# Revit family: ВентКлиматСтрой Вентилятор систем дымоудаления осевой ВО-13-284ДУ
name_source: partatom
category: Оборудование
units: mm (PartAtom-declared; Revit-internal decimal feet)

## family parameters
Всегда вертикально = Да
Заголовок OmniClass = Fans for Air Ductwork
На основе рабочей плоскости = Нет
Номер OmniClass = 23.75.35.17.11
Общий = Нет
При загрузке вырезать с полостями = Нет
Размер круглого соединителя = Использовать диаметр
Тип детали = Вставляется
Точка расчета площади = Да

## types (22) — shared parameters
ADSK_Версия Revit = 2019
ADSK_Версия семейства = rev.1
ADSK_Единица измерения = шт.
ADSK_Классификация нагрузок = Прочее
ADSK_Количество = 1
ADSK_Количество фаз числовое = 3
ADSK_Коэффициент мощности = 0.8
ADSK_Предел огнестойкости = 120
Poles = 3
Размер символа УГО = 0.4
zero-valued in all types: ADSK_Материал тип подсчета

## per-type parameters (varying)
| type | A | B | B1 | D | D1 | De | H | L | R1 | Re | b | d | f | h | l | n | Полюсов |
| ВО 13-284-12К/*-4ДУ 4 полюса | 475 мм | 480 мм | 380 мм | 400 мм | 440 мм | 404 мм | 555 мм | 550 мм | 220 мм | 202 мм | 199 мм | 10 мм | 30 мм | 240 мм | 548 мм | 8 | 4 |
| ВО 13-284-12К/*-4ДУ 2 полюса | 475 мм | 480 мм | 380 мм | 400 мм | 440 мм | 404 мм | 555 мм | 550 мм | 220 мм | 202 мм | 199 мм | 10 мм | 30 мм | 240 мм | 548 мм | 8 | 2 |
| ВО 13-284-12К/*-4,5ДУ 4 полюса | 540 мм | 560 мм | 460 мм | 450 мм | 490 мм | 454 мм | 620 мм | 650 мм | 245 мм | 227 мм | 232 мм | 10 мм | 30 мм | 280 мм | 648 мм | 8 | 4 |
| ВО 13-284-12К/*-4,5ДУ 2 полюса | 540 мм | 560 мм | 460 мм | 450 мм | 490 мм | 454 мм | 620 мм | 650 мм | 245 мм | 227 мм | 232 мм | 10 мм | 30 мм | 280 мм | 648 мм | 8 | 2 |
| ВО 13-284-12К/*-5ДУ 4 полюса | 600 мм | 600 мм | 500 мм | 500 мм | 540 мм | 504 мм | 675 мм | 740 мм | 270 мм | 252 мм | 249 мм | 10 мм | 30 мм | 300 мм | 738 мм | 12 | 4 |
| ВО 13-284-12К/*-5ДУ 2 полюса | 600 мм | 600 мм | 500 мм | 500 мм | 540 мм | 504 мм | 675 мм | 740 мм | 270 мм | 252 мм | 249 мм | 10 мм | 30 мм | 300 мм | 738 мм | 12 | 2 |
| ВО 13-284-12К/*-5,6ДУ 4 полюса | 600 мм | 600 мм | 500 мм | 560 мм | 600 мм | 564 мм | 745 мм | 740 мм | 300 мм | 282 мм | 249 мм | 10 мм | 35 мм | 300 мм | 738 мм | 12 | 4 |
| ВО 13-284-12К/*-5,6ДУ 2 полюса | 600 мм | 600 мм | 500 мм | 560 мм | 600 мм | 564 мм | 745 мм | 740 мм | 300 мм | 282 мм | 249 мм | 10 мм | 35 мм | 300 мм | 738 мм | 12 | 2 |
| ВО 13-284-12К/*-6,3ДУ 4 полюса | 720 мм | 760 мм | 660 мм | 630 мм | 670 мм | 634 мм | 830 мм | 840 мм | 335 мм | 317 мм | 315 мм | 10 мм | 35 мм | 400 мм | 838 мм | 12 | 4 |
| ВО 13-284-12К/*-6,3ДУ 2 полюса | 720 мм | 760 мм | 660 мм | 630 мм | 670 мм | 634 мм | 830 мм | 840 мм | 335 мм | 317 мм | 315 мм | 10 мм | 35 мм | 400 мм | 838 мм | 12 | 2 |
| ВО 13-284-12К/*-7,1ДУ 6 полюсов | 900 мм | 900 мм | 800 мм | 710 мм | 750 мм | 714 мм | 925 мм | 930 мм | 375 мм | 357 мм | 373 мм | 10 мм | 35 мм | 450 мм | 928 мм | 16 | 6 |
| ВО 13-284-12К/*-7,1ДУ 4 полюса | 900 мм | 900 мм | 800 мм | 710 мм | 750 мм | 714 мм | 925 мм | 930 мм | 375 мм | 357 мм | 373 мм | 10 мм | 35 мм | 450 мм | 928 мм | 16 | 4 |
| ВО 13-284-12К/*-8ДУ 6 полюсов | 1000 мм | 1000 мм | 900 мм | 800 мм | 840 мм | 804 мм | 1020 мм | 1110 мм | 420 мм | 402 мм | 414 мм | 10 мм | 35 мм | 500 мм | 1108 мм | 16 | 6 |
| ВО 13-284-12К/*-8ДУ 4 полюса | 1000 мм | 1000 мм | 900 мм | 800 мм | 840 мм | 804 мм | 1020 мм | 1110 мм | 420 мм | 402 мм | 414 мм | 10 мм | 35 мм | 500 мм | 1108 мм | 16 | 4 |
| ВО 13-284-12К/*-9ДУ 6 полюсов | 1100 мм | 1100 мм | 1000 мм | 900 мм | 950 мм | 904 мм | 1135 мм | 1140 мм | 475 мм | 452 мм | 456 мм | 10 мм | 40 мм | 550 мм | 1138 мм | 16 | 6 |
| ВО 13-284-12К/*-9ДУ 4 полюса | 1100 мм | 1100 мм | 1000 мм | 900 мм | 950 мм | 904 мм | 1135 мм | 1140 мм | 475 мм | 452 мм | 456 мм | 10 мм | 40 мм | 550 мм | 1138 мм | 16 | 4 |
| ВО 13-284-12К/*-10ДУ 6 полюсов | 1250 мм | 1250 мм | 1150 мм | 1000 мм | 1050 мм | 1004 мм | 1245 мм | 1150 мм | 525 мм | 502 мм | 518 мм | 10 мм | 40 мм | 625 мм | 1148 мм | 16 | 6 |
| ВО 13-284-12К/*-10ДУ 4 полюса | 1250 мм | 1250 мм | 1150 мм | 1000 мм | 1050 мм | 1004 мм | 1245 мм | 1150 мм | 525 мм | 502 мм | 518 мм | 10 мм | 40 мм | 625 мм | 1148 мм | 16 | 4 |
| ВО 13-284-12К/*-11,2ДУ 6 полюсов | 1300 мм | 1300 мм | 1200 мм | 1120 мм | 1170 мм | 1124 мм | 1385 мм | 1120 мм | 585 мм | 562 мм | 538 мм | 12 мм | 50 мм | 650 мм | 1118 мм | 20 | 6 |
| ВО 13-284-12К/*-11,2ДУ 4 полюса | 1300 мм | 1300 мм | 1200 мм | 1120 мм | 1170 мм | 1124 мм | 1385 мм | 1120 мм | 585 мм | 562 мм | 538 мм | 12 мм | 50 мм | 650 мм | 1118 мм | 20 | 4 |
| ВО 13-284-12К/*-12,5ДУ 8 полюсов | 1400 мм | 1400 мм | 1300 мм | 1250 мм | 1300 мм | 1254 мм | 1550 мм | 1170 мм | 650 мм | 627 мм | 580 мм | 12 мм | 50 мм | 700 мм | 1168 мм | 20 | 8 |
| ВО 13-284-12К/*-12,5ДУ 6 полюсов | 1400 мм | 1400 мм | 1300 мм | 1250 мм | 1300 мм | 1254 мм | 1550 мм | 1170 мм | 650 мм | 627 мм | 580 мм | 12 мм | 50 мм | 700 мм | 1168 мм | 20 | 6 |

## geometry (parser evidence)
native form markers: Sweep x3
no freeform markers — native parametric forms only
